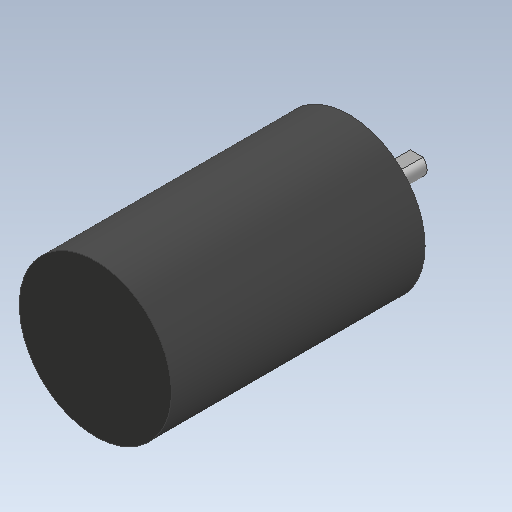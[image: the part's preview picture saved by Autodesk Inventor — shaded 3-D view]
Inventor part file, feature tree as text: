
AUTODESK INVENTOR PART (.ipt)
format: ipt  version: 2021 (Build 250183000, 183)  size: 110,592 bytes
history: native  units: mm
features: sketch x4, other x3
ambient origin geometry x8: Origin, YZ Plane, XZ Plane, XY Plane, X Axis, Y Axis, Z Axis, Center Point
bodies: Solid1 (feature_tree)
feature tree (7):
  other  "silnik 3660.ipt"
  other  "Solid1::silnik 3660.ipt"
  other  "TaggingFeature1"
  sketch  "Sketch1"  dims[d0=10.0mm]
  sketch  "Sketch2"
  sketch  "Sketch3"
  sketch  "Sketch4"
